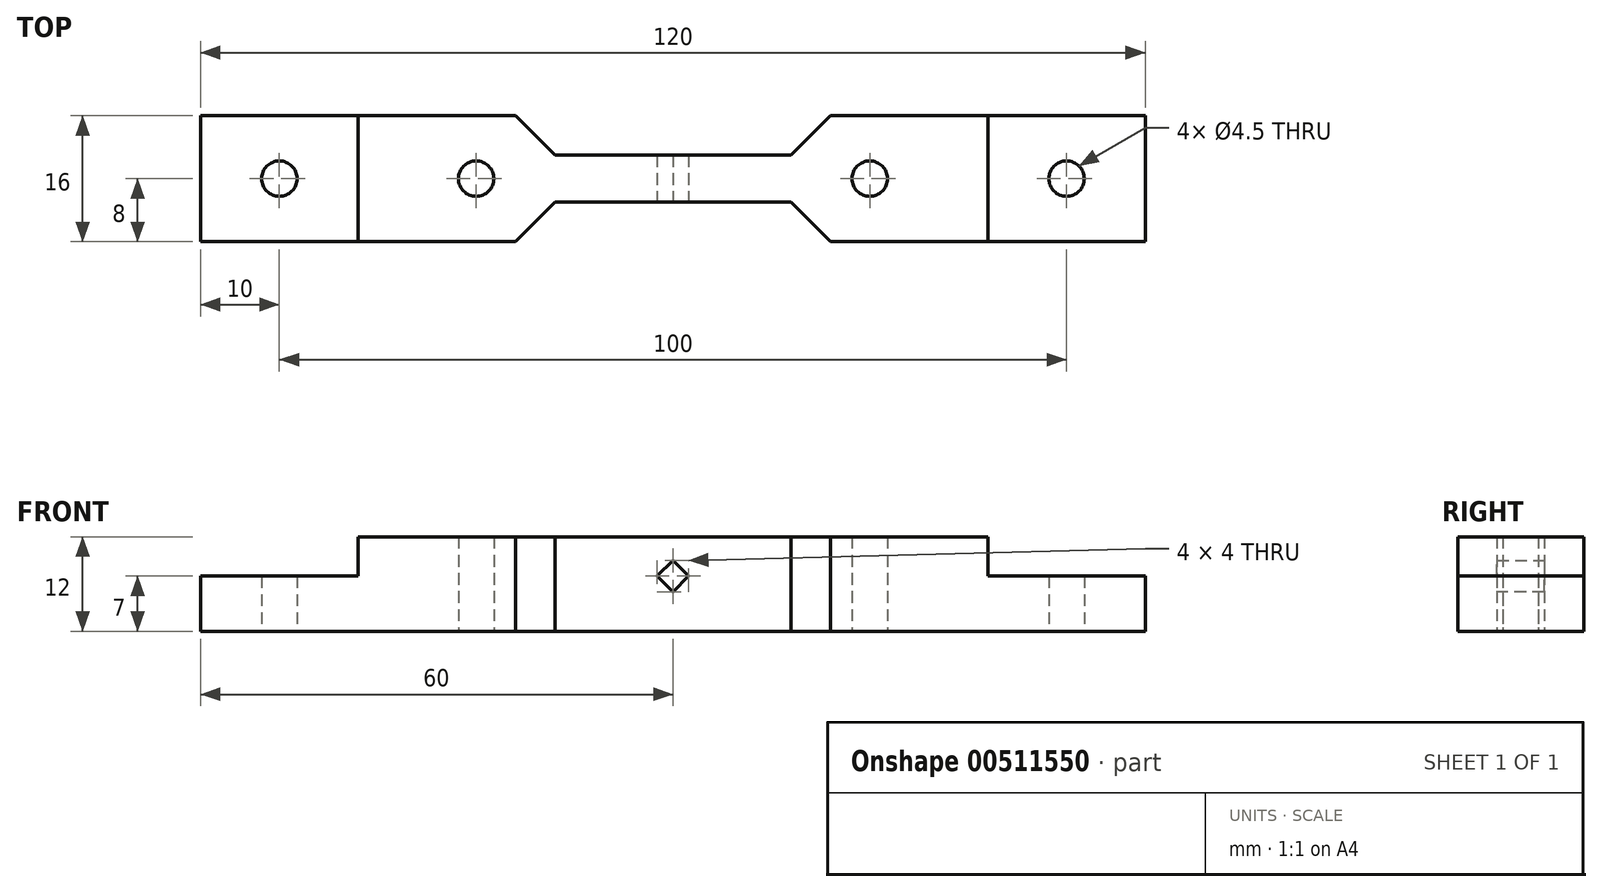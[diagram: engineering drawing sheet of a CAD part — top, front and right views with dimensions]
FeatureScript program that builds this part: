
annotation { "Feature Type Name" : "Feature", "Feature Type Description" : "" }
export const myFeature = defineFeature(function(context is Context, id is Id, definition is map)
    precondition{}
    {
        {
            var Q0;
            Q0=qCreatedBy(makeId("Top.planeOp"),FACE);
            var sketch = newSketch(context, id + "F0", { "sketchPlane" : qUnion([Q0])});
            skLineSegment(sketch, "E0", {"start": v(0, 0) * mm, "end": v(0, 3) * mm});
            skLineSegment(sketch, "E1", {"start": v(0, 3) * mm, "end": v(-15, 3) * mm});
            skLineSegment(sketch, "E2", {"start": v(-15, 3) * mm, "end": v(-20, 8) * mm});
            skLineSegment(sketch, "E3", {"start": v(-20, 8) * mm, "end": v(-30, 8) * mm});
            skLineSegment(sketch, "E4", {"start": v(-30, -8) * mm, "end": v(-20, -8) * mm});
            skLineSegment(sketch, "E5", {"start": v(-20, -8) * mm, "end": v(-15, -3) * mm});
            skLineSegment(sketch, "E6", {"start": v(-15, -3) * mm, "end": v(0, -3) * mm});
            skLineSegment(sketch, "E7", {"start": v(0, -3) * mm, "end": v(0, 0) * mm});
            skLineSegment(sketch, "E8", {"start": v(0, 12.5) * mm, "end": v(0, -12.97) * mm, "construction": true});
            skLineSegment(sketch, "E9.MirrorCS", {"start": v(0, 3) * mm, "end": v(15, 3) * mm});
            skLineSegment(sketch, "E10.MirrorCS", {"start": v(15, 3) * mm, "end": v(20, 8) * mm});
            skLineSegment(sketch, "E11.MirrorCS", {"start": v(20, 8) * mm, "end": v(30, 8) * mm});
            skLineSegment(sketch, "E12.MirrorCS", {"start": v(30, -8) * mm, "end": v(20, -8) * mm});
            skLineSegment(sketch, "E13.MirrorCS", {"start": v(20, -8) * mm, "end": v(15, -3) * mm});
            skLineSegment(sketch, "E14.MirrorCS", {"start": v(15, -3) * mm, "end": v(0, -3) * mm});
            skCircle(sketch, "E15", {"center": v(-25, 0) * mm, "radius": 2.25 * mm});
            skCircle(sketch, "E16", {"center": v(25, 0) * mm, "radius": 2.25 * mm});
            skPoint(sketch, "E17.endSnap0", {"position": v(-7.5, -3) * mm});
            skLineSegment(sketch, "E18", {"start": v(-54.39, 8) * mm, "end": v(-60, 8) * mm});
            skLineSegment(sketch, "E19", {"start": v(-60, 8) * mm, "end": v(-60, -8) * mm});
            skLineSegment(sketch, "E20", {"start": v(-60, -8) * mm, "end": v(-54.39, -8) * mm});
            skLineSegment(sketch, "E21", {"start": v(53.18, 8) * mm, "end": v(60, 8) * mm});
            skLineSegment(sketch, "E22", {"start": v(60, -8) * mm, "end": v(53.18, -8) * mm});
            skCircle(sketch, "E23", {"center": v(50, 0) * mm, "radius": 2.25 * mm});
            skCircle(sketch, "E24", {"center": v(-50, 0) * mm, "radius": 2.25 * mm});
            skLineSegment(sketch, "E25", {"start": v(-54.39, 8) * mm, "end": v(-30, 8) * mm});
            skLineSegment(sketch, "E26", {"start": v(-54.39, -8) * mm, "end": v(-30, -8) * mm});
            skLineSegment(sketch, "E27", {"start": v(53.18, -8) * mm, "end": v(30, -8) * mm});
            skLineSegment(sketch, "E28", {"start": v(30, 8) * mm, "end": v(53.18, 8) * mm});
            skLineSegment(sketch, "E29", {"start": v(60, 8) * mm, "end": v(60, -8) * mm});
            skSolve(sketch);
        }
        {
            var Q0;
            Q0=makeQuery(id+"F0.imprint","IMPRINT",FACE,{"disambiguationData":[TD([[makeQuery(id+"F0.imprint","IMPRINT",EDGE,{"derivedFrom":sQuery(id+"F0.wireOp",EDGE,"E0")}),1.0]])]});
            var Q1;
            Q1=makeQuery(id+"F0.imprint","IMPRINT",FACE,{"disambiguationData":[TD([[makeQuery(id+"F0.imprint","IMPRINT",EDGE,{"derivedFrom":sQuery(id+"F0.wireOp",EDGE,"E0")}),-1.0]])]});
            extrude(context, id + "F1", {"entities" : qUnion([Q0, Q1]), "depth" : 7 * mm, "offsetDistance" : 25 * mm});
        }
        {
            var Q0;
            Q0=qCreatedBy(makeId("Front.planeOp"),FACE);
            var sketch = newSketch(context, id + "F2", { "sketchPlane" : qUnion([Q0])});
            skLineSegment(sketch, "E30.0", {"start": v(-15, 7) * mm, "end": v(15, 7) * mm});
            skLineSegment(sketch, "E31.0.0", {"start": v(-15, 0) * mm, "end": v(15, 0) * mm});
            skLineSegment(sketch, "E31.0.1", {"start": v(15, 0) * mm, "end": v(15, 7) * mm});
            skLineSegment(sketch, "E31.0.2", {"start": v(15, 7) * mm, "end": v(-15, 7) * mm});
            skLineSegment(sketch, "E31.0.3", {"start": v(-15, 7) * mm, "end": v(-15, 0) * mm});
            skLineSegment(sketch, "E32", {"start": v(0, 0) * mm, "end": v(-15, 0) * mm});
            skLineSegment(sketch, "E33", {"start": v(-15, 7) * mm, "end": v(-2, 7) * mm});
            skLineSegment(sketch, "E34", {"start": v(-2, 7) * mm, "end": v(0, 5) * mm});
            skLineSegment(sketch, "E35", {"start": v(0, 5) * mm, "end": v(2, 7) * mm});
            skLineSegment(sketch, "E36", {"start": v(2, 7) * mm, "end": v(15, 7) * mm});
            skLineSegment(sketch, "E37", {"start": v(15, 0) * mm, "end": v(0, 0) * mm});
            skLineSegment(sketch, "E38", {"start": v(0, 0) * mm, "end": v(0, 13.7) * mm, "construction": true});
            skPoint(sketch, "E39", {"position": v(0, 7) * mm});
            skLineSegment(sketch, "E40", {"start": v(-2, 7) * mm, "end": v(0, 9) * mm});
            skLineSegment(sketch, "E41", {"start": v(0, 9) * mm, "end": v(2, 7) * mm});
            skLineSegment(sketch, "E42", {"start": v(-2, 7) * mm, "end": v(2, 7) * mm});
            skLineSegment(sketch, "E43", {"start": v(15, 7) * mm, "end": v(35, 7) * mm});
            skLineSegment(sketch, "E44", {"start": v(35, 7) * mm, "end": v(35, 12) * mm});
            skLineSegment(sketch, "E45", {"start": v(35, 12) * mm, "end": v(-35, 12) * mm});
            skLineSegment(sketch, "E46", {"start": v(-35, 12) * mm, "end": v(-35, 7) * mm});
            skLineSegment(sketch, "E47", {"start": v(-35, 7) * mm, "end": v(-15, 7) * mm});
            skSolve(sketch);
        }
        {
            var Q0;
            {var subQ2=sQuery(id+"F2.wireOp",EDGE,"E34");Q0=makeQuery(id+"F2.imprint","IMPRINT",FACE,{"disambiguationData":[TD([[makeQuery(id+"F2.imprint","IMPRINT",EDGE,{"derivedFrom":subQ2}),1.0]])]});}
            extrude(context, id + "F3", {"entities" : qUnion([Q0]), "operationType" : NewBodyOperationType.REMOVE, "endBound" : BoundingType.SYMMETRIC, "oppositeDirection" : true, "depth" : 6 * mm, "offsetDistance" : 25 * mm});
        }
        {
            var Q0;
            {var subQ0=sQuery(id+"F2.wireOp",EDGE,"E40");Q0=makeQuery(id+"F2.imprint","IMPRINT",FACE,{"disambiguationData":[TD([[makeQuery(id+"F2.imprint","IMPRINT",EDGE,{"derivedFrom":subQ0}),1.0]])]});}
            extrude(context, id + "F4", {"entities" : qUnion([Q0]), "endBound" : BoundingType.SYMMETRIC, "depth" : 6 * mm, "offsetDistance" : 25 * mm});
        }
        {
            var Q0;
            {var subQ0=sQuery(id+"F0.wireOp",EDGE,"E26");var subQ1=sQuery(id+"F0.wireOp",EDGE,"E20");var subQ2=sQuery(id+"F0.wireOp",EDGE,"E4");var subQ3=sQuery(id+"F0.wireOp",EDGE,"E24");var subQ4=sQuery(id+"F0.wireOp",EDGE,"E25");var subQ5=sQuery(id+"F0.wireOp",EDGE,"E18");var subQ6=sQuery(id+"F0.wireOp",EDGE,"E3");var subQ7=sQuery(id+"F0.wireOp",EDGE,"E2");var subQ8=sQuery(id+"F0.wireOp",EDGE,"E19");var subQ9=sQuery(id+"F0.wireOp",EDGE,"E9.MirrorCS");var subQ10=sQuery(id+"F0.wireOp",EDGE,"E1");var subQ11=sQuery(id+"F0.wireOp",EDGE,"E5");var subQ12=sQuery(id+"F0.wireOp",EDGE,"E14.MirrorCS");var subQ13=sQuery(id+"F0.wireOp",EDGE,"E6");var subQ14=sQuery(id+"F0.wireOp",EDGE,"E15");Q0=makeQuery(id+"F3.boolean.opBoolean","SPLIT",FACE,{"disambiguationData":[TD([makeQuery(id+"F1.opExtrude","SWEPT_FACE",FACE,{"disambiguationData":[OSD([subQ7])]})])],"derivedFrom":makeQuery(id+"F1.opExtrude","CAP_FACE",FACE,{"disambiguationData":[OSD([subQ10,subQ7,subQ6,subQ2,subQ11,subQ13,subQ9,sQuery(id+"F0.wireOp",EDGE,"E10.MirrorCS"),sQuery(id+"F0.wireOp",EDGE,"E11.MirrorCS"),sQuery(id+"F0.wireOp",EDGE,"E12.MirrorCS"),sQuery(id+"F0.wireOp",EDGE,"E13.MirrorCS"),subQ12,subQ14,sQuery(id+"F0.wireOp",EDGE,"E16"),subQ5,subQ8,subQ1,sQuery(id+"F0.wireOp",EDGE,"E21"),sQuery(id+"F0.wireOp",EDGE,"E22"),sQuery(id+"F0.wireOp",EDGE,"E23"),subQ3,subQ4,subQ0,sQuery(id+"F0.wireOp",EDGE,"E27"),sQuery(id+"F0.wireOp",EDGE,"E28"),sQuery(id+"F0.wireOp",EDGE,"E29")])],"isStart":false})});}
            var sketch = newSketch(context, id + "F5", { "sketchPlane" : qUnion([Q0])});
            skLineSegment(sketch, "E48.0.0", {"start": v(15, 3) * mm, "end": v(2, 3) * mm});
            skLineSegment(sketch, "E48.0.1", {"start": v(2, 3) * mm, "end": v(2, -3) * mm});
            skLineSegment(sketch, "E48.0.2", {"start": v(2, -3) * mm, "end": v(15, -3) * mm});
            skLineSegment(sketch, "E48.0.3", {"start": v(15, -3) * mm, "end": v(20, -8) * mm});
            skLineSegment(sketch, "E48.0.4", {"start": v(20, -8) * mm, "end": v(60, -8) * mm});
            skLineSegment(sketch, "E48.0.5", {"start": v(60, -8) * mm, "end": v(60, 8) * mm});
            skLineSegment(sketch, "E48.0.6", {"start": v(60, 8) * mm, "end": v(20, 8) * mm});
            skLineSegment(sketch, "E48.0.7", {"start": v(20, 8) * mm, "end": v(15, 3) * mm});
            skLineSegment(sketch, "E49", {"start": v(-15, 3) * mm, "end": v(-20, 8) * mm});
            skLineSegment(sketch, "E50", {"start": v(-20, 8) * mm, "end": v(-40, 8) * mm});
            skLineSegment(sketch, "E51", {"start": v(-40, 8) * mm, "end": v(-40, -8) * mm});
            skLineSegment(sketch, "E52", {"start": v(-40, -8) * mm, "end": v(-20, -8) * mm});
            skLineSegment(sketch, "E53", {"start": v(-20, -8) * mm, "end": v(-15, -3) * mm});
            skLineSegment(sketch, "E54", {"start": v(-15, -3) * mm, "end": v(-15, 3) * mm});
            skLineSegment(sketch, "E55", {"start": v(15, 3) * mm, "end": v(15, -3) * mm});
            skLineSegment(sketch, "E56", {"start": v(20, -8) * mm, "end": v(40, -8) * mm});
            skLineSegment(sketch, "E57", {"start": v(40, -8) * mm, "end": v(40, 8) * mm});
            skLineSegment(sketch, "E58", {"start": v(40, 8) * mm, "end": v(20, 8) * mm});
            skCircle(sketch, "E59.0", {"center": v(-25, 0) * mm, "radius": 2.25 * mm});
            skCircle(sketch, "E59.1", {"center": v(25, 0) * mm, "radius": 2.25 * mm});
            skSolve(sketch);
        }
        {
            var Q0;
            Q0=makeQuery(id+"F5.imprint","IMPRINT",FACE,{"disambiguationData":[TD([[makeQuery(id+"F5.imprint","IMPRINT",EDGE,{"derivedFrom":sQuery(id+"F5.wireOp",EDGE,"E49")}),1.0]])]});
            var Q1;
            Q1=makeQuery(id+"F5.imprint","IMPRINT",FACE,{"disambiguationData":[TD([[makeQuery(id+"F5.imprint","IMPRINT",EDGE,{"derivedFrom":sQuery(id+"F5.wireOp",EDGE,"E48.0.3")}),1.0]])]});
            extrude(context, id + "F6", {"entities" : qUnion([Q0, Q1]), "operationType" : NewBodyOperationType.ADD, "depth" : 5 * mm, "offsetDistance" : 25 * mm});
        }
        {
            var Q0;
            Q0=makeQuery(id+"F5.imprint","IMPRINT",FACE,{"disambiguationData":[TD([[makeQuery(id+"F5.imprint","IMPRINT",EDGE,{"derivedFrom":sQuery(id+"F5.wireOp",EDGE,"E59.0")}),1.0]])]});
            var Q1;
            Q1=makeQuery(id+"F5.imprint","IMPRINT",FACE,{"disambiguationData":[TD([[makeQuery(id+"F5.imprint","IMPRINT",EDGE,{"derivedFrom":sQuery(id+"F5.wireOp",EDGE,"E59.1")}),1.0]])]});
            var Q2;
            Q2=sQuery(id+"F5.wireOp",EDGE,"E59.0");
            var Q3;
            Q3=sQuery(id+"F5.wireOp",EDGE,"E59.1");
            extrude(context, id + "F7", {"entities" : qUnion([Q0, Q1]), "operationType" : NewBodyOperationType.REMOVE, "surfaceEntities" : qUnion([Q2, Q3]), "depth" : 5 * mm, "offsetDistance" : 25 * mm});
        }
    });
